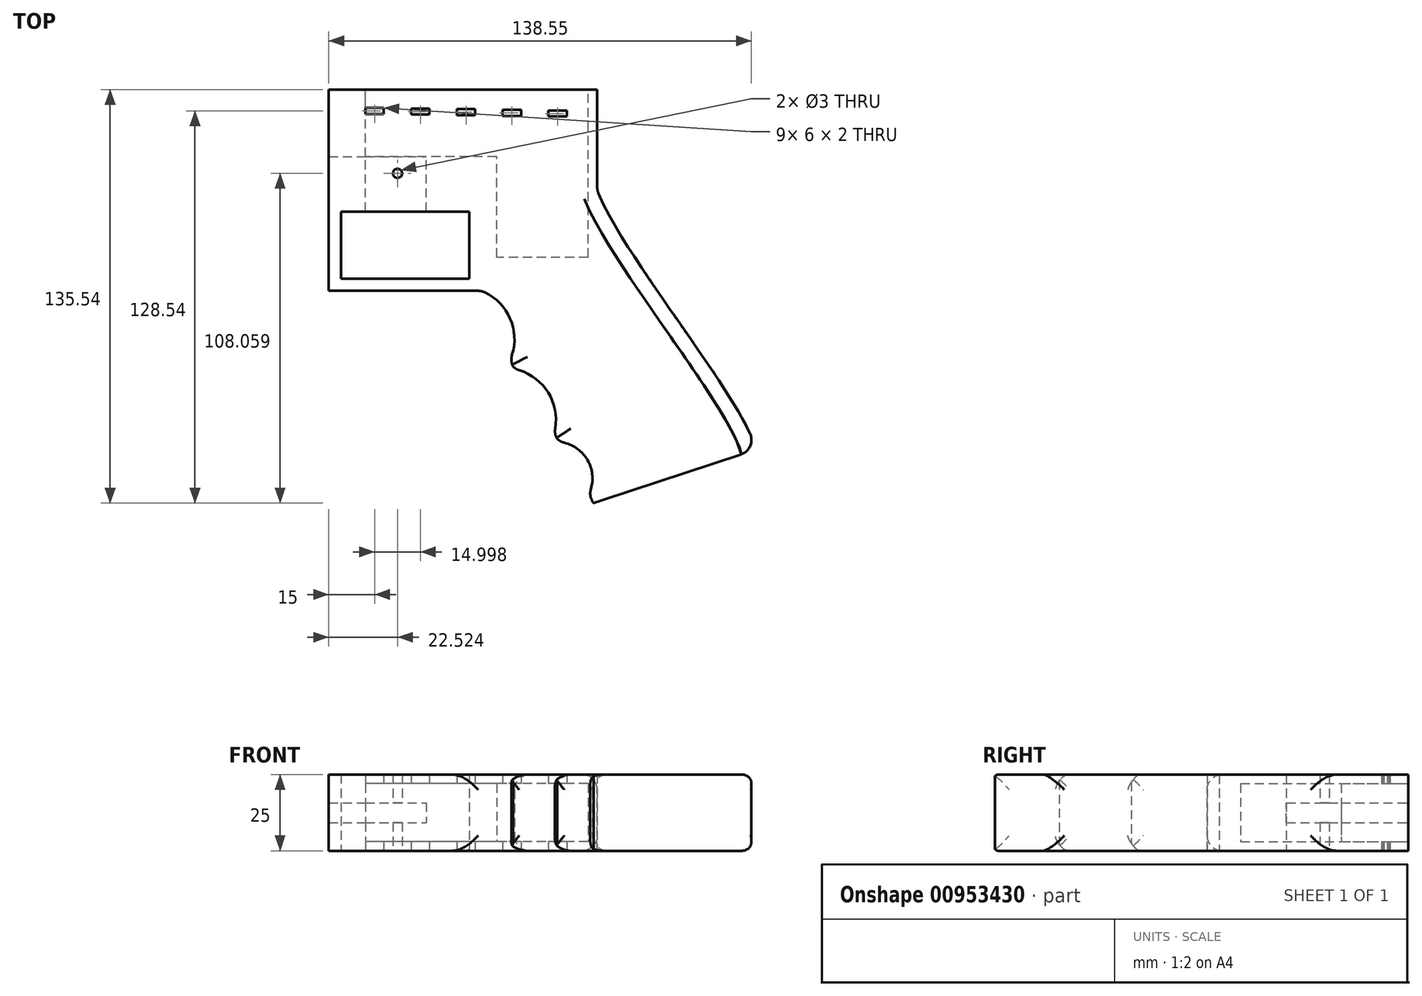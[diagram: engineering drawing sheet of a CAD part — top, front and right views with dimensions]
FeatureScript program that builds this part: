
annotation { "Feature Type Name" : "Feature", "Feature Type Description" : "" }
export const myFeature = defineFeature(function(context is Context, id is Id, definition is map)
    precondition{}
    {
        {
            var Q0;
            Q0=qCreatedBy(makeId("Top.planeOp"),FACE);
            var sketch = newSketch(context, id + "F0", { "sketchPlane" : qUnion([Q0])});
            skLineSegment(sketch, "E0.bottom", {"start": v(44, 33) * mm, "end": v(-44, 33) * mm});
            skLineSegment(sketch, "E0.top", {"start": v(44, -33) * mm, "end": v(-44, -33) * mm});
            skLineSegment(sketch, "E0.left", {"start": v(44, 33) * mm, "end": v(44, -33) * mm});
            skLineSegment(sketch, "E0.right", {"start": v(-44, 33) * mm, "end": v(-44, -33) * mm});
            skPoint(sketch, "E0.middle", {"position": v(0, 0) * mm});
            skLineSegment(sketch, "E1.bottom", {"start": v(-40, -29) * mm, "end": v(2, -29) * mm});
            skLineSegment(sketch, "E1.top", {"start": v(-40, -7) * mm, "end": v(2, -7) * mm});
            skLineSegment(sketch, "E1.left", {"start": v(-40, -29) * mm, "end": v(-40, -7) * mm});
            skLineSegment(sketch, "E1.right", {"start": v(2, -29) * mm, "end": v(2, -7) * mm});
            skLineSegment(sketch, "E2.bottom", {"start": v(-32, 27) * mm, "end": v(-26, 27) * mm});
            skLineSegment(sketch, "E2.top", {"start": v(-32, 25) * mm, "end": v(-26, 25) * mm});
            skLineSegment(sketch, "E2.left", {"start": v(-32, 27) * mm, "end": v(-32, 25) * mm});
            skLineSegment(sketch, "E2.right", {"start": v(-26, 27) * mm, "end": v(-26, 25) * mm});
            skLineSegment(sketch, "E3.1.0.0", {"start": v(-17, 26.79) * mm, "end": v(-11, 26.79) * mm});
            skLineSegment(sketch, "E3.1.0.1", {"start": v(-11, 26.79) * mm, "end": v(-11, 24.79) * mm});
            skLineSegment(sketch, "E3.1.0.2", {"start": v(-17, 24.79) * mm, "end": v(-11, 24.79) * mm});
            skLineSegment(sketch, "E3.1.0.3", {"start": v(-17, 26.79) * mm, "end": v(-17, 24.79) * mm});
            skLineSegment(sketch, "E3.2.0.0", {"start": v(-2, 26.58) * mm, "end": v(4, 26.58) * mm});
            skLineSegment(sketch, "E3.2.0.1", {"start": v(4, 26.58) * mm, "end": v(4, 24.58) * mm});
            skLineSegment(sketch, "E3.2.0.2", {"start": v(-2, 24.58) * mm, "end": v(4, 24.58) * mm});
            skLineSegment(sketch, "E3.2.0.3", {"start": v(-2, 26.58) * mm, "end": v(-2, 24.58) * mm});
            skLineSegment(sketch, "E3.3.0.0", {"start": v(13, 26.37) * mm, "end": v(19, 26.37) * mm});
            skLineSegment(sketch, "E3.3.0.1", {"start": v(19, 26.37) * mm, "end": v(19, 24.37) * mm});
            skLineSegment(sketch, "E3.3.0.2", {"start": v(13, 24.37) * mm, "end": v(19, 24.37) * mm});
            skLineSegment(sketch, "E3.3.0.3", {"start": v(13, 26.37) * mm, "end": v(13, 24.37) * mm});
            skLineSegment(sketch, "E3.4.0.0", {"start": v(28, 26.16) * mm, "end": v(34, 26.16) * mm});
            skLineSegment(sketch, "E3.4.0.1", {"start": v(34, 26.16) * mm, "end": v(34, 24.16) * mm});
            skLineSegment(sketch, "E3.4.0.2", {"start": v(28, 24.16) * mm, "end": v(34, 24.16) * mm});
            skLineSegment(sketch, "E3.4.0.3", {"start": v(28, 26.16) * mm, "end": v(28, 24.16) * mm});
            skLineSegment(sketch, "E3.direction1", {"start": v(-32, 27) * mm, "end": v(-17, 26.79) * mm, "construction": true});
            skFitSpline(sketch, "E4", {"points": [v(44, 0) * mm, v(96, -85) * mm], "startDerivative": vector(22.94, -62.1) * mm, "endDerivative": vector(10.88, -48) * mm});
            skLineSegment(sketch, "E5", {"start": v(96, -85) * mm, "end": v(42.82, -102.54) * mm});
            skLineSegment(sketch, "E6", {"start": v(41, -100.16) * mm, "end": v(42.82, -102.54) * mm});
            skArc(sketch, "E7", {"start": v(15.15, -56.27) * mm, "mid": v(15.67, -42.63) * mm, "end": v(6, -33) * mm});
            skLineSegment(sketch, "E8", {"start": v(15.15, -56.27) * mm, "end": v(16.97, -58.65) * mm});
            skArc(sketch, "E9", {"start": v(29.76, -80.13) * mm, "mid": v(28.07, -66.59) * mm, "end": v(16.97, -58.65) * mm});
            skLineSegment(sketch, "E10", {"start": v(29.76, -80.13) * mm, "end": v(31.58, -82.5) * mm});
            skArc(sketch, "E11", {"start": v(41, -100.16) * mm, "mid": v(41.02, -88.81) * mm, "end": v(31.58, -82.5) * mm});
            skSolve(sketch);
        }
        {
            var Q0;
            {var subQ0=sQuery(id+"F0.wireOp",EDGE,"E4");Q0=makeQuery(id+"F0.imprint","IMPRINT",FACE,{"disambiguationData":[TD([[makeQuery(id+"F0.imprint","IMPRINT",EDGE,{"derivedFrom":subQ0}),-1.0]])]});}
            var Q1;
            {var subQ1=sQuery(id+"F0.wireOp",EDGE,"E0.bottom");Q1=makeQuery(id+"F0.imprint","IMPRINT",FACE,{"disambiguationData":[TD([[makeQuery(id+"F0.imprint","IMPRINT",EDGE,{"derivedFrom":subQ1}),1.0]])]});}
            extrude(context, id + "F1", {"entities" : qUnion([Q0, Q1]), "depth" : 25 * mm, "offsetDistance" : 25 * mm});
        }
        {
            var Q0;
            Q0=makeQuery(id+"F1.opExtrude","SWEPT_FACE",FACE,{"disambiguationData":[OSD([sQuery(id+"F0.wireOp",EDGE,"E0.bottom")])]});
            var sketch = newSketch(context, id + "F2", { "sketchPlane" : qUnion([Q0])});
            skLineSegment(sketch, "E12.bottom", {"start": v(-41, 22) * mm, "end": v(32, 22) * mm});
            skLineSegment(sketch, "E12.top", {"start": v(-41, 3) * mm, "end": v(32, 3) * mm});
            skLineSegment(sketch, "E12.left", {"start": v(-41, 22) * mm, "end": v(-41, 3) * mm});
            skLineSegment(sketch, "E12.right", {"start": v(32, 22) * mm, "end": v(32, 3) * mm});
            skLineSegment(sketch, "E13", {"start": v(-11, 22) * mm, "end": v(-11, 3) * mm});
            skLineSegment(sketch, "E14.bottom", {"start": v(44, 15.75) * mm, "end": v(12, 15.75) * mm});
            skLineSegment(sketch, "E14.top", {"start": v(44, 9.25) * mm, "end": v(12, 9.25) * mm});
            skLineSegment(sketch, "E14.left", {"start": v(44, 15.75) * mm, "end": v(44, 9.25) * mm});
            skLineSegment(sketch, "E14.right", {"start": v(12, 15.75) * mm, "end": v(12, 9.25) * mm});
            skLineSegment(sketch, "E15", {"start": v(23.56, 22) * mm, "end": v(23.56, 15.75) * mm, "construction": true});
            skLineSegment(sketch, "E16", {"start": v(23.71, 9.25) * mm, "end": v(23.71, 3) * mm, "construction": true});
            skSolve(sketch);
        }
        {
            var Q0;
            {var subQ0=sQuery(id+"F2.wireOp",EDGE,"E12.left");Q0=makeQuery(id+"F2.imprint","IMPRINT",FACE,{"disambiguationData":[TD([[makeQuery(id+"F2.imprint","IMPRINT",EDGE,{"derivedFrom":subQ0}),1.0]])]});}
            var Q1;
            {var subQ5=sQuery(id+"F2.wireOp",EDGE,"E14.left");Q1=makeQuery(id+"F2.imprint","IMPRINT",FACE,{"disambiguationData":[TD([[makeQuery(id+"F2.imprint","IMPRINT",EDGE,{"derivedFrom":subQ5}),-1.0]])]});}
            var Q2;
            {var subQ5=sQuery(id+"F2.wireOp",EDGE,"E14.right");Q2=makeQuery(id+"F2.imprint","IMPRINT",FACE,{"disambiguationData":[TD([[makeQuery(id+"F2.imprint","IMPRINT",EDGE,{"derivedFrom":subQ5}),1.0]])]});}
            var Q3;
            {var subQ9=sQuery(id+"F2.wireOp",EDGE,"E13");Q3=makeQuery(id+"F2.imprint","IMPRINT",FACE,{"disambiguationData":[TD([[makeQuery(id+"F2.imprint","IMPRINT",EDGE,{"derivedFrom":subQ9}),1.0]])]});}
            extrude(context, id + "F3", {"entities" : qUnion([Q0, Q1, Q2, Q3]), "operationType" : NewBodyOperationType.REMOVE, "oppositeDirection" : true, "depth" : 22 * mm, "offsetDistance" : 25 * mm});
        }
        {
            var Q0;
            {var subQ0=sQuery(id+"F2.wireOp",EDGE,"E12.left");Q0=makeQuery(id+"F2.imprint","IMPRINT",FACE,{"disambiguationData":[TD([[makeQuery(id+"F2.imprint","IMPRINT",EDGE,{"derivedFrom":subQ0}),1.0]])]});}
            extrude(context, id + "F4", {"entities" : qUnion([Q0]), "operationType" : NewBodyOperationType.REMOVE, "oppositeDirection" : true, "depth" : 55 * mm, "offsetDistance" : 25 * mm});
        }
        {
            var Q0;
            {var subQ5=sQuery(id+"F2.wireOp",EDGE,"E14.right");Q0=makeQuery(id+"F2.imprint","IMPRINT",FACE,{"disambiguationData":[TD([[makeQuery(id+"F2.imprint","IMPRINT",EDGE,{"derivedFrom":subQ5}),1.0]])]});}
            var Q1;
            Q1=makeQuery(id+"F1.opExtrude","SWEPT_FACE",FACE,{"disambiguationData":[OSD([sQuery(id+"F0.wireOp",EDGE,"E1.top")])]});
            extrude(context, id + "F5", {"entities" : qUnion([Q0]), "operationType" : NewBodyOperationType.REMOVE, "endBound" : BoundingType.UP_TO_SURFACE, "oppositeDirection" : true, "depth" : 25 * mm, "endBoundEntityFace" : qUnion([Q1]), "offsetDistance" : 25 * mm});
        }
        {
            var Q0;
            Q0=qCreatedBy(makeId("Top.planeOp"),FACE);
            var sketch = newSketch(context, id + "F6", { "sketchPlane" : qUnion([Q0])});
            skCircle(sketch, "E17", {"center": v(-21.48, 5.52) * mm, "radius": 1.5 * mm});
            skSolve(sketch);
        }
        {
            var Q0;
            Q0=makeQuery(id+"F6.imprint","IMPRINT",FACE,{"disambiguationData":[TD([[makeQuery(id+"F6.imprint","IMPRINT",EDGE,{"derivedFrom":sQuery(id+"F6.wireOp",EDGE,"E17")}),1.0]])]});
            extrude(context, id + "F7", {"entities" : qUnion([Q0]), "operationType" : NewBodyOperationType.REMOVE, "endBound" : BoundingType.THROUGH_ALL, "depth" : 25 * mm, "offsetDistance" : 25 * mm});
        }
        {
            var Q0;
            Q0=makeQuery(id+"F1.opExtrude","SWEPT_FACE",FACE,{"disambiguationData":[OSD([sQuery(id+"F0.wireOp",EDGE,"E4")])]});
            fillet(context, id + "F8", {"entities" : qUnion([Q0]), "radius" : 5 * mm, "tangentPropagation" : true, "allowEdgeOverflow" : false});
        }
        {
            var Q0;
            Q0=makeQuery(id+"F1.opExtrude","SWEPT_FACE",FACE,{"disambiguationData":[OSD([sQuery(id+"F0.wireOp",EDGE,"E7")])]});
            var Q1;
            Q1=makeQuery(id+"F1.opExtrude","SWEPT_FACE",FACE,{"disambiguationData":[OSD([sQuery(id+"F0.wireOp",EDGE,"E9")])]});
            var Q2;
            Q2=makeQuery(id+"F1.opExtrude","SWEPT_FACE",FACE,{"disambiguationData":[OSD([sQuery(id+"F0.wireOp",EDGE,"E11")])]});
            fillet(context, id + "F9", {"entities" : qUnion([Q0, Q1, Q2]), "radius" : 5 * mm, "tangentPropagation" : true, "allowEdgeOverflow" : false});
        }
    });
